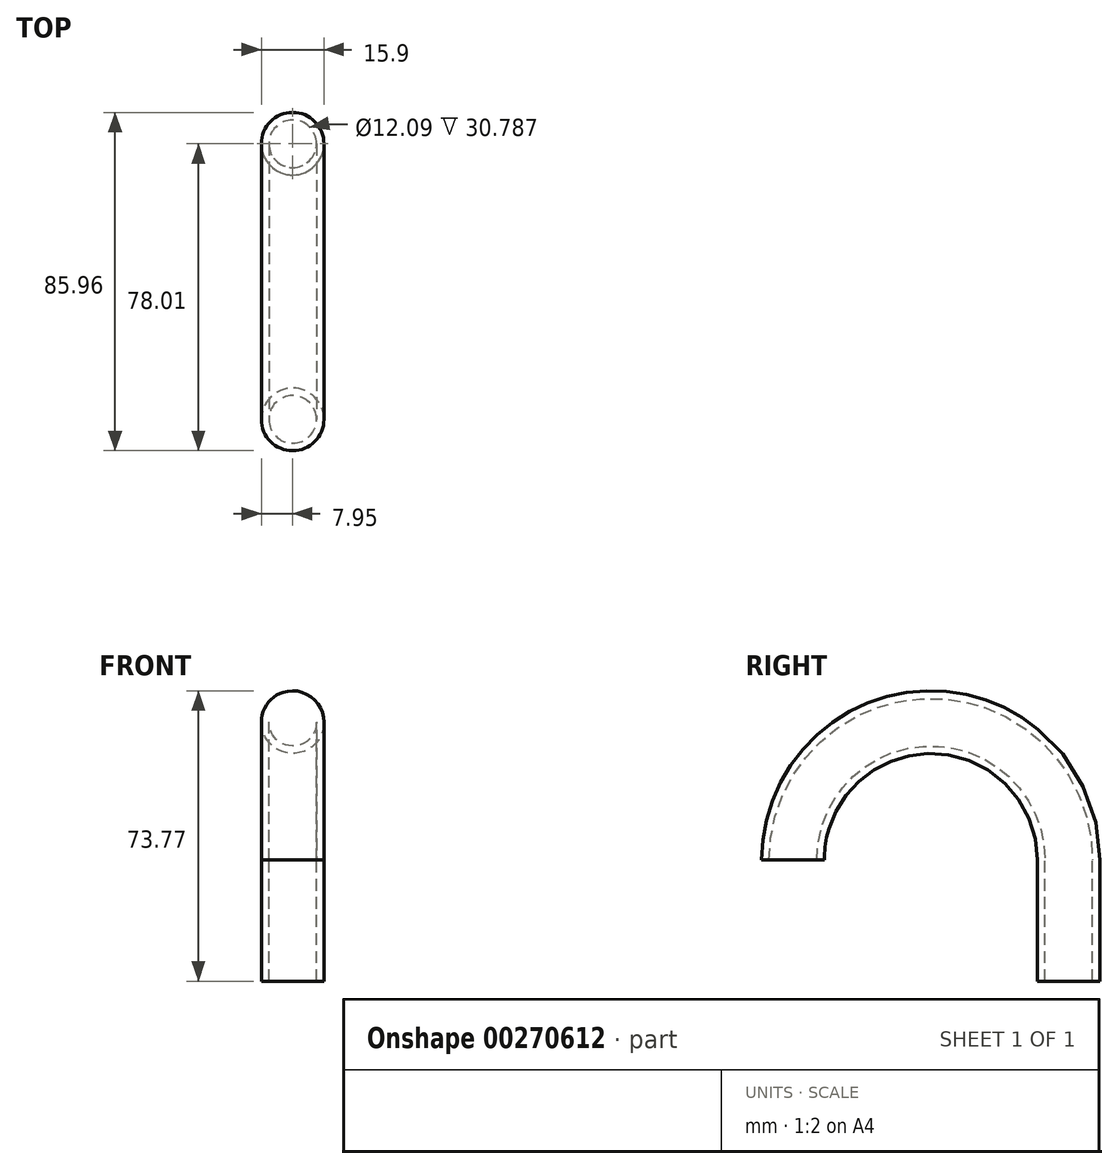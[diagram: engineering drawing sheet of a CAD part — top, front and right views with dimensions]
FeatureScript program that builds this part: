
annotation { "Feature Type Name" : "Feature", "Feature Type Description" : "" }
export const myFeature = defineFeature(function(context is Context, id is Id, definition is map)
    precondition{}
    {
        {
            var Q0;
            Q0=qCreatedBy(makeId("Top.planeOp"),FACE);
            var sketch = newSketch(context, id + "F0", { "sketchPlane" : qUnion([Q0])});
            skCircle(sketch, "E0", {"center": v(0, 0) * mm, "radius": 7.95 * mm});
            skSolve(sketch);
        }
        {
            var Q0;
            Q0=qCreatedBy(makeId("Right.planeOp"),FACE);
            var sketch = newSketch(context, id + "F1", { "sketchPlane" : qUnion([Q0])});
            skLineSegment(sketch, "E1", {"start": v(0, 0) * mm, "end": v(0, 30.79) * mm});
            skArc(sketch, "E2", {"start": v(0, 30.79) * mm, "mid": v(-35.03, 65.81) * mm, "end": v(-70.05, 30.79) * mm});
            skSolve(sketch);
        }
        {
            var Q0;
            Q0=makeQuery(id+"F0.imprint","IMPRINT",FACE,{"disambiguationData":[TD([[makeQuery(id+"F0.imprint","IMPRINT",EDGE,{"derivedFrom":sQuery(id+"F0.wireOp",EDGE,"E0")}),1.0]])]});
            var Q1;
            Q1=sQuery(id+"F1.wireOp",EDGE,"E1");
            var Q2;
            Q2=sQuery(id+"F1.wireOp",EDGE,"E2");
            sweep(context, id + "F2", {"profiles" : qUnion([Q0]), "path" : qUnion([Q1, Q2])});
        }
        {
            var Q0;
            Q0=qCreatedBy(makeId("Top.planeOp"),FACE);
            var sketch = newSketch(context, id + "F3", { "sketchPlane" : qUnion([Q0])});
            skCircle(sketch, "E3", {"center": v(0, 0) * mm, "radius": 6.05 * mm});
            skSolve(sketch);
        }
        {
            var Q0;
            Q0=makeQuery(id+"F3.imprint","IMPRINT",FACE,{"disambiguationData":[TD([[makeQuery(id+"F3.imprint","IMPRINT",EDGE,{"derivedFrom":sQuery(id+"F3.wireOp",EDGE,"E3")}),1.0]])]});
            var Q1;
            Q1=sQuery(id+"F1.wireOp",EDGE,"E1");
            var Q2;
            Q2=sQuery(id+"F1.wireOp",EDGE,"E2");
            sweep(context, id + "F4", {"operationType" : NewBodyOperationType.REMOVE, "profiles" : qUnion([Q0]), "path" : qUnion([Q1, Q2])});
        }
    });
